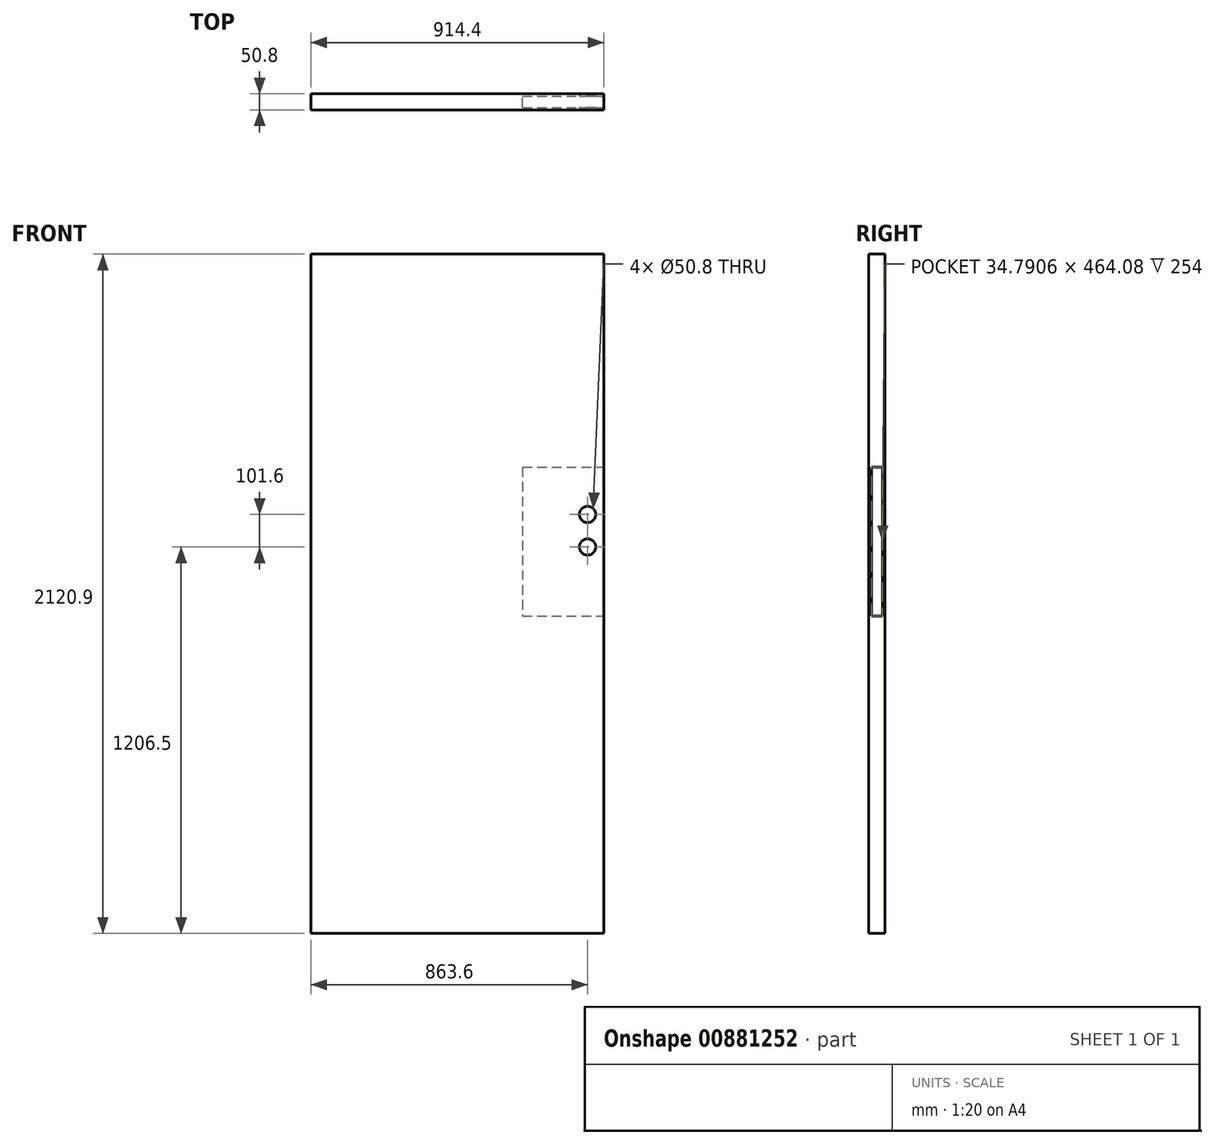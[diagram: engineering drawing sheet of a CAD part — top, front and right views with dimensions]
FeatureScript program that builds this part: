
annotation { "Feature Type Name" : "Feature", "Feature Type Description" : "" }
export const myFeature = defineFeature(function(context is Context, id is Id, definition is map)
    precondition{}
    {
        {
            var Q0;
            Q0=qCreatedBy(makeId("Front.planeOp"),FACE);
            var sketch = newSketch(context, id + "F0", { "sketchPlane" : qUnion([Q0])});
            skLineSegment(sketch, "E0.bottom", {"start": v(-457.2, 1060.45) * mm, "end": v(457.2, 1060.45) * mm});
            skLineSegment(sketch, "E0.top", {"start": v(-457.2, -1060.45) * mm, "end": v(457.2, -1060.45) * mm});
            skLineSegment(sketch, "E0.left", {"start": v(-457.2, 1060.45) * mm, "end": v(-457.2, -1060.45) * mm});
            skLineSegment(sketch, "E0.right", {"start": v(457.2, 1060.45) * mm, "end": v(457.2, -1060.45) * mm});
            skSolve(sketch);
        }
        {
            var Q0;
            Q0=qSketchRegion(id+"F0",true);
            extrude(context, id + "F1", {"entities" : qUnion([Q0]), "depth" : 50.8 * mm, "offsetDistance" : 25.4 * mm});
        }
        {
            var Q0;
            Q0=makeQuery(id+"F1.opExtrude","CAP_FACE",FACE,{"disambiguationData":[OSD([sQuery(id+"F0.wireOp",EDGE,"E0.bottom"),sQuery(id+"F0.wireOp",EDGE,"E0.top"),sQuery(id+"F0.wireOp",EDGE,"E0.left"),sQuery(id+"F0.wireOp",EDGE,"E0.right")])],"isStart":false});
            var sketch = newSketch(context, id + "F2", { "sketchPlane" : qUnion([Q0])});
            skCircle(sketch, "E1", {"center": v(406.4, 247.65) * mm, "radius": 25.4 * mm});
            skCircle(sketch, "E2", {"center": v(406.4, 146.05) * mm, "radius": 25.4 * mm});
            skSolve(sketch);
        }
        {
            var Q0;
            Q0=qSketchRegion(id+"F2",true);
            extrude(context, id + "F3", {"entities" : qUnion([Q0]), "operationType" : NewBodyOperationType.REMOVE, "endBound" : BoundingType.THROUGH_ALL, "oppositeDirection" : true, "depth" : 25.4 * mm, "offsetDistance" : 25.4 * mm});
        }
        {
            var Q0;
            Q0=makeQuery(id+"F1.opExtrude","SWEPT_FACE",FACE,{"disambiguationData":[OSD([sQuery(id+"F0.wireOp",EDGE,"E0.right")])]});
            var sketch = newSketch(context, id + "F4", { "sketchPlane" : qUnion([Q0])});
            skLineSegment(sketch, "E3.bottom", {"start": v(-42.75, 395.2) * mm, "end": v(-7.96, 395.2) * mm});
            skLineSegment(sketch, "E3.top", {"start": v(-42.75, -68.88) * mm, "end": v(-7.96, -68.88) * mm});
            skLineSegment(sketch, "E3.left", {"start": v(-42.75, 395.2) * mm, "end": v(-42.75, -68.88) * mm});
            skLineSegment(sketch, "E3.right", {"start": v(-7.96, 395.2) * mm, "end": v(-7.96, -68.88) * mm});
            skSolve(sketch);
        }
        {
            var Q0;
            Q0=makeQuery(id+"F4.imprint","IMPRINT",FACE,{"disambiguationData":[TD([[makeQuery(id+"F4.imprint","IMPRINT",EDGE,{"derivedFrom":sQuery(id+"F4.wireOp",EDGE,"E3.bottom")}),-1.0]])]});
            extrude(context, id + "F5", {"entities" : qUnion([Q0]), "operationType" : NewBodyOperationType.REMOVE, "depth" : -254 * mm, "offsetDistance" : 25.4 * mm});
        }
    });
